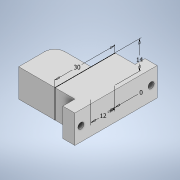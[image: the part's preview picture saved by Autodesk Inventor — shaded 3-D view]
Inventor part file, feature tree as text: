
AUTODESK INVENTOR PART (.ipt)
format: ipt  version: 2020.3 (Build 243373000, 373)  size: 271,360 bytes
history: native  units: mm
features: extrude x3, sketch x2, fillet x1
ambient origin geometry x8: Origin, YZ Plane, XZ Plane, XY Plane, X Axis, Y Axis, Z Axis, Center Point
bodies: Body1 (feature_tree)
feature tree (6):
  sketch  "Sketch1"  dims[d12=14.0mm d13=30.0mm]
  extrude  "Extrusion6"  Depth=30.0mm
  extrude  "Extrusion7"  TaperAngle=0.0deg  [1 undecoded]
  fillet  "Fillet2"  Radius=10.0mm
  extrude  "Extrusion9"  Depth=10.0mm TaperAngle=0.0deg
  sketch  "Sketch7"  dims[d14=12.0mm d15=0.0mm d16=10.0mm d17=0.0mm d18=10.0mm d19=0.0mm d29=18.0mm d30=0.0mm d31=5.0mm d32=41.0mm d33=5.0mm d34=14.0mm d35=3.0mm d36=3.0mm d37=3.0mm d38=35.0mm d39=6.0mm d40=0.0mm]
note: 1 required parameter value undecoded (feature->parameter linkage not recoverable at this tier; creation-order binding heuristic only, values carry confidence <= 0.55)
